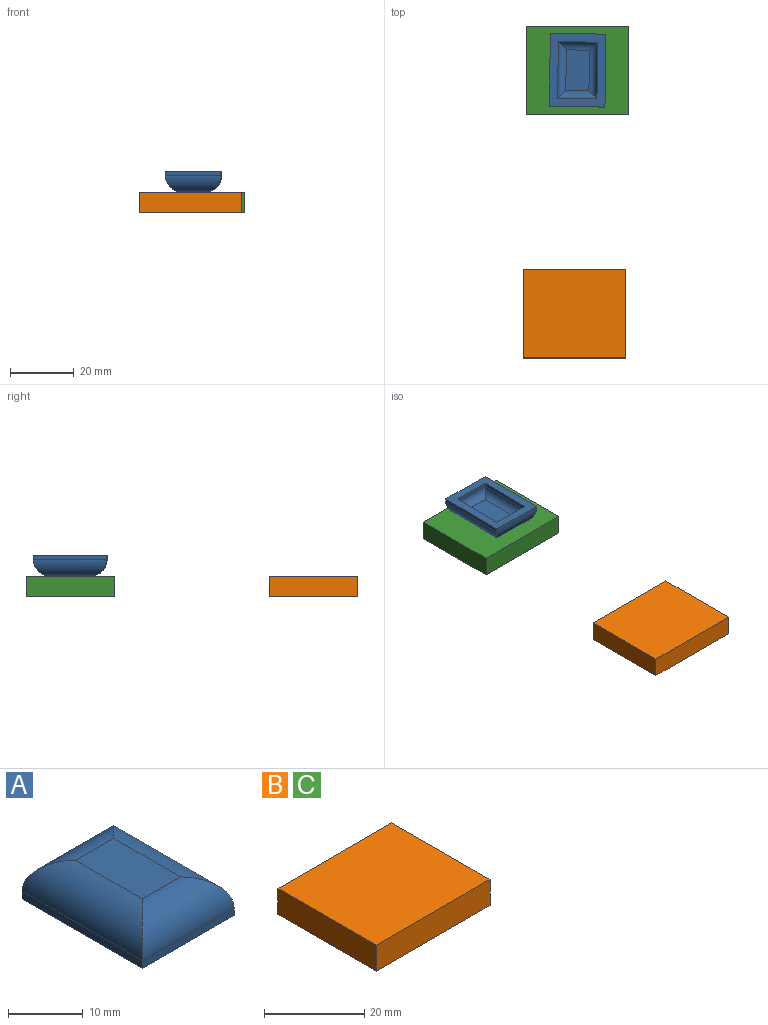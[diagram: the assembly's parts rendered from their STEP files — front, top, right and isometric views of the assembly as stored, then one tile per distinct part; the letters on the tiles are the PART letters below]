
ASSEMBLY  parts=3 mates=1
PART A: 19 faces, bbox 17.4x22.8x6.4 mm
  f0: plane 22.83x1.27mm, normal (-1,0,0), area 29mm2, adj f1,f3,f5,f6
  f1: plane 17.4x1.27mm, normal (0,-1,0), area 22.1mm2, adj f0,f2,f5,f8
  f2: plane 22.83x1.27mm, normal (1,0,0), area 29mm2, adj f1,f3,f5,f9
  f3: plane 17.4x1.27mm, normal (0,1,0), area 22.1mm2, adj f0,f2,f5,f7
  f4: plane 12.67x7.24mm, normal (0,0,1), area 91.8mm2, adj f6,f7,f8,f9
  f5: plane 22.83x17.4mm, normal (0,0,-1), area 178.6mm2, adj f0,f1,f2,f3,f10,f11,f12,f13
  f6: cylinder r=5.08mm len=22.83mm, axis (0,1,0), area 152.8mm2, adj f0,f4,f7,f8
  f7: cylinder r=5.08mm len=17.4mm, axis (1,0,0), area 109.4mm2, adj f3,f4,f6,f9
  f8: cylinder r=5.08mm len=17.4mm, axis (-1,0,0), area 109.4mm2, adj f1,f4,f6,f9
  f9: cylinder r=5.08mm len=22.83mm, axis (0,-1,0), area 152.8mm2, adj f2,f4,f7,f8
  f10: plane 17.75x1.27mm, normal (1,0,0), area 22.5mm2, adj f5,f11,f13,f15
  f11: plane 12.32x1.27mm, normal (0,1,0), area 15.6mm2, adj f5,f10,f12,f17
  f12: plane 17.75x1.27mm, normal (-1,0,0), area 22.5mm2, adj f5,f11,f13,f18
  f13: plane 12.32x1.27mm, normal (0,-1,0), area 15.6mm2, adj f5,f10,f12,f16
  f14: plane 12.67x7.24mm, normal (0,0,-1), area 91.8mm2, adj f15,f16,f17,f18
  f15: cylinder r=2.54mm len=17.75mm, axis (0,1,0), area 63.5mm2, adj f10,f14,f16,f17
  f16: cylinder r=2.54mm len=12.32mm, axis (1,0,0), area 41.8mm2, adj f13,f14,f15,f18
  f17: cylinder r=2.54mm len=12.32mm, axis (-1,0,0), area 41.8mm2, adj f11,f14,f15,f18
  f18: cylinder r=2.54mm len=17.75mm, axis (0,-1,0), area 63.5mm2, adj f12,f14,f16,f17
PART B: 6 faces, bbox 32.1x27.7x6.4 mm
  f0: plane 32.12x6.35mm, normal (0,1,0), area 204mm2, adj f1,f3,f4,f5
  f1: plane 27.71x6.35mm, normal (-1,0,0), area 176mm2, adj f0,f2,f4,f5
  f2: plane 32.12x6.35mm, normal (0,-1,0), area 204mm2, adj f1,f3,f4,f5
  f3: plane 27.71x6.35mm, normal (1,0,0), area 176mm2, adj f0,f2,f4,f5
  f4: plane 32.12x27.71mm, normal (0,0,1), area 890.2mm2, adj f0,f1,f2,f3
  f5: plane 32.12x27.71mm, normal (0,0,-1), area 890.2mm2, adj f0,f1,f2,f3
PART C: same geometry as B
PLACE A rot(axis=(-0.01,-1,0),180deg) t=(-22.53,36.29,12.7)mm
PLACE B t=(-1.02,-76.19,0)mm
PLACE C at identity fixed
MATE revolute A.f4 <-> C.f4  axis (0,0,-1) through (16.06,-8.78,6.35)mm
